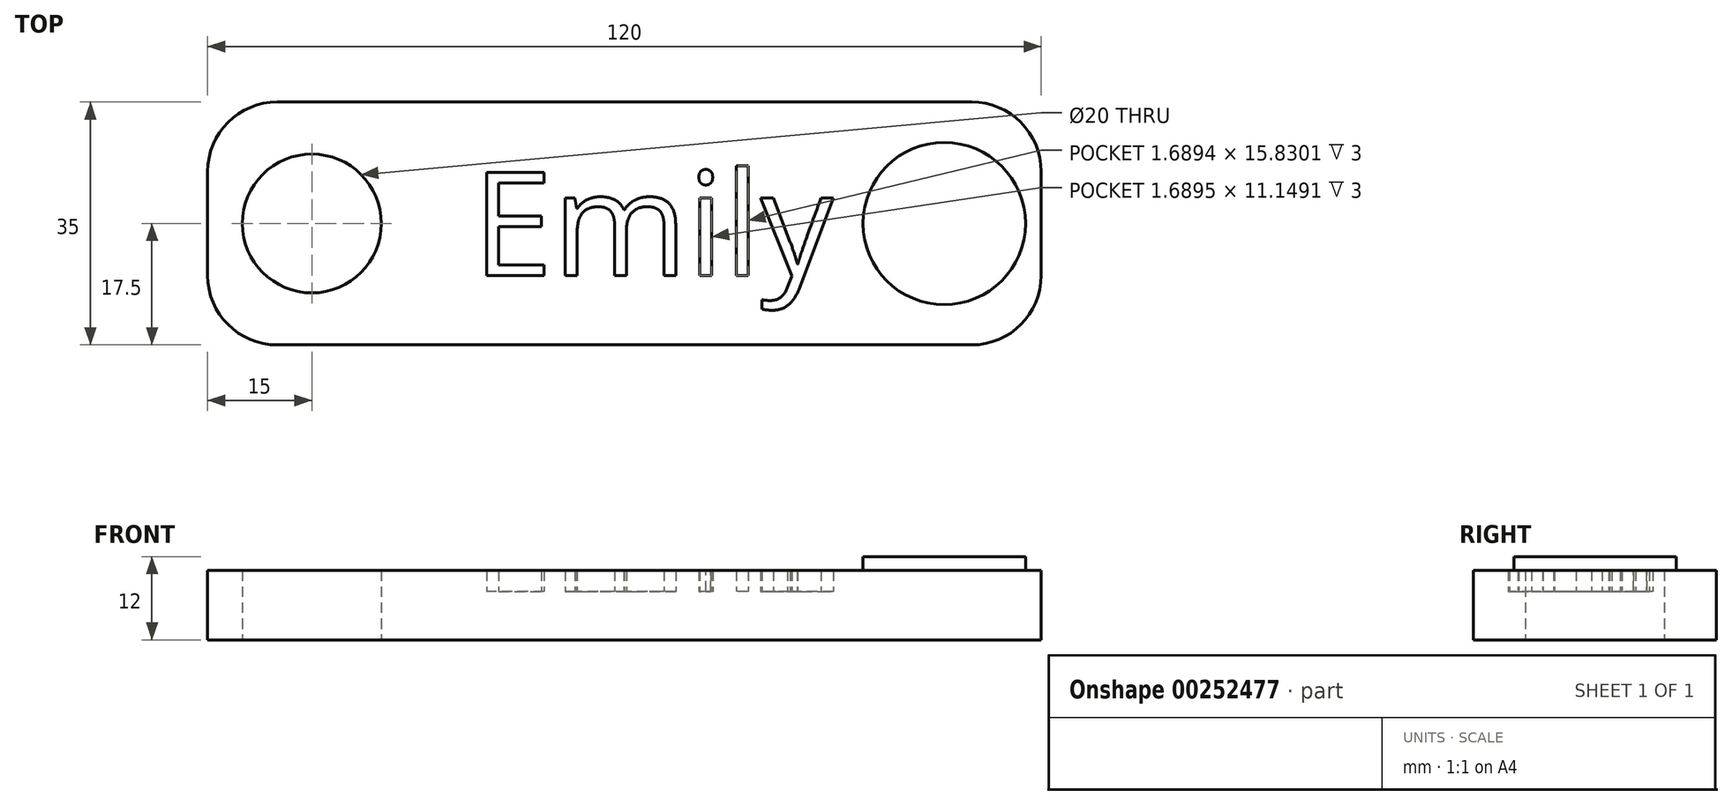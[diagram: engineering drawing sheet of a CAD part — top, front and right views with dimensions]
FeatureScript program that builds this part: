
annotation { "Feature Type Name" : "Feature", "Feature Type Description" : "" }
export const myFeature = defineFeature(function(context is Context, id is Id, definition is map)
    precondition{}
    {
        {
            var Q0;
            Q0=qCreatedBy(makeId("Top.planeOp"),FACE);
            var sketch = newSketch(context, id + "F0", { "sketchPlane" : qUnion([Q0])});
            skLineSegment(sketch, "E0.bottom", {"start": v(60, -17.5) * mm, "end": v(-60, -17.5) * mm});
            skLineSegment(sketch, "E0.top", {"start": v(60, 17.5) * mm, "end": v(-60, 17.5) * mm});
            skLineSegment(sketch, "E0.left", {"start": v(60, -17.5) * mm, "end": v(60, 17.5) * mm});
            skLineSegment(sketch, "E0.right", {"start": v(-60, -17.5) * mm, "end": v(-60, 17.5) * mm});
            skPoint(sketch, "E0.middle", {"position": v(0, 0) * mm});
            skCircle(sketch, "E1", {"center": v(-45, 0) * mm, "radius": 10 * mm});
            skPoint(sketch, "E1.centerSnap0", {"position": v(-60, 0) * mm});
            skSolve(sketch);
        }
        {
            var Q0;
            Q0=makeQuery(id+"F0.imprint","IMPRINT",FACE,{"disambiguationData":[TD([[makeQuery(id+"F0.imprint","IMPRINT",EDGE,{"derivedFrom":sQuery(id+"F0.wireOp",EDGE,"E0.bottom")}),-1.0]])]});
            extrude(context, id + "F1", {"entities" : qUnion([Q0]), "depth" : 5 * mm});
        }
        {
            var Q0;
            Q0=makeQuery(id+"F1.opExtrude","SWEPT_EDGE",EDGE,{"disambiguationData":[OSD([sQuery(id+"F0.wireOp",EDGE,"E0.bottom"),sQuery(id+"F0.wireOp",EDGE,"E0.right")])]});
            var Q1;
            Q1=makeQuery(id+"F1.opExtrude","SWEPT_EDGE",EDGE,{"disambiguationData":[OSD([sQuery(id+"F0.wireOp",EDGE,"E0.bottom"),sQuery(id+"F0.wireOp",EDGE,"E0.left")])]});
            var Q2;
            Q2=makeQuery(id+"F1.opExtrude","SWEPT_EDGE",EDGE,{"disambiguationData":[OSD([sQuery(id+"F0.wireOp",EDGE,"E0.top"),sQuery(id+"F0.wireOp",EDGE,"E0.right")])]});
            var Q3;
            Q3=makeQuery(id+"F1.opExtrude","SWEPT_EDGE",EDGE,{"disambiguationData":[OSD([sQuery(id+"F0.wireOp",EDGE,"E0.top"),sQuery(id+"F0.wireOp",EDGE,"E0.left")])]});
            fillet(context, id + "F2", {"entities" : qUnion([Q0, Q1, Q2, Q3]), "radius" : 10 * mm, "tangentPropagation" : true, "allowEdgeOverflow" : false});
        }
        {
            var Q0;
            Q0=makeQuery(id+"F1.opExtrude","CAP_FACE",FACE,{"disambiguationData":[OSD([sQuery(id+"F0.wireOp",EDGE,"E0.bottom"),sQuery(id+"F0.wireOp",EDGE,"E0.top"),sQuery(id+"F0.wireOp",EDGE,"E0.left"),sQuery(id+"F0.wireOp",EDGE,"E0.right"),sQuery(id+"F0.wireOp",EDGE,"E1")])],"isStart":false});
            var sketch = newSketch(context, id + "F3", { "sketchPlane" : qUnion([Q0])});
            skText(sketch, "E2", { "text": "Emily", "fontName": "OpenSans-Regular.ttf"});
            const initialGuessF3  = {"E2": [-0.02189, -0.0075, 1, 0, 0.015]};
            skSetInitialGuess(sketch, initialGuessF3);
            skSolve(sketch);
        }
        {
            var Q0;
            Q0 = qSketchRegion(id + "F3", true);
            extrude(context, id + "F4", {"entities" : qUnion([Q0]), "operationType" : NewBodyOperationType.ADD, "depth" : 2 * mm});
        }
        {
            var Q0;
            Q0=makeQuery(id+"F1.opExtrude","CAP_FACE",FACE,{"disambiguationData":[OSD([sQuery(id+"F0.wireOp",EDGE,"E0.bottom"),sQuery(id+"F0.wireOp",EDGE,"E0.top"),sQuery(id+"F0.wireOp",EDGE,"E0.left"),sQuery(id+"F0.wireOp",EDGE,"E0.right"),sQuery(id+"F0.wireOp",EDGE,"E1")])],"isStart":false});
            var sketch = newSketch(context, id + "F5", { "sketchPlane" : qUnion([Q0])});
            skSolve(sketch);
        }
        {
            var Q0;
            Q0 = qSketchRegion(id + "F5", true);
            var Q1;
            {var subQ2=sQuery(id+"F0.wireOp",EDGE,"E1");Q1=makeQuery(id+"F5.imprint","IMPRINT",FACE,{"disambiguationData":[TD([[makeQuery(id+"F5.imprint","IMPRINT",EDGE,{"derivedFrom":makeQuery(id+"F1.opExtrude","CAP_EDGE",EDGE,{"disambiguationData":[OSD([subQ2])],"isStart":false})}),-1.0]])]});}
            extrude(context, id + "F6", {"entities" : qUnion([Q0, Q1]), "operationType" : NewBodyOperationType.ADD, "depth" : 5 * mm});
        }
        {
            var Q0;
            Q0=makeQuery(id+"F6.opExtrude","CAP_FACE",FACE,{"disambiguationData":[OSD([sQuery(id+"F0.wireOp",EDGE,"E0.bottom"),sQuery(id+"F0.wireOp",EDGE,"E0.top"),sQuery(id+"F0.wireOp",EDGE,"E0.left"),sQuery(id+"F0.wireOp",EDGE,"E0.right"),sQuery(id+"F0.wireOp",EDGE,"E1"),sQuery(id+"F3.wireOp",EDGE,"E2.sketch_text.stroke-0"),sQuery(id+"F3.wireOp",EDGE,"E2.sketch_text.stroke-1"),sQuery(id+"F3.wireOp",EDGE,"E2.sketch_text.stroke-2"),sQuery(id+"F3.wireOp",EDGE,"E2.sketch_text.stroke-3"),sQuery(id+"F3.wireOp",EDGE,"E2.sketch_text.stroke-4"),sQuery(id+"F3.wireOp",EDGE,"E2.sketch_text.stroke-5"),sQuery(id+"F3.wireOp",EDGE,"E2.sketch_text.stroke-6"),sQuery(id+"F3.wireOp",EDGE,"E2.sketch_text.stroke-7"),sQuery(id+"F3.wireOp",EDGE,"E2.sketch_text.stroke-8"),sQuery(id+"F3.wireOp",EDGE,"E2.sketch_text.stroke-9"),sQuery(id+"F3.wireOp",EDGE,"E2.sketch_text.stroke-10"),sQuery(id+"F3.wireOp",EDGE,"E2.sketch_text.stroke-11"),sQuery(id+"F3.wireOp",EDGE,"E2.sketch_text.stroke-12"),sQuery(id+"F3.wireOp",EDGE,"E2.sketch_text.stroke-13"),sQuery(id+"F3.wireOp",EDGE,"E2.sketch_text.stroke-14"),sQuery(id+"F3.wireOp",EDGE,"E2.sketch_text.stroke-15"),sQuery(id+"F3.wireOp",EDGE,"E2.sketch_text.stroke-16"),sQuery(id+"F3.wireOp",EDGE,"E2.sketch_text.stroke-17"),sQuery(id+"F3.wireOp",EDGE,"E2.sketch_text.stroke-18"),sQuery(id+"F3.wireOp",EDGE,"E2.sketch_text.stroke-19"),sQuery(id+"F3.wireOp",EDGE,"E2.sketch_text.stroke-20"),sQuery(id+"F3.wireOp",EDGE,"E2.sketch_text.stroke-21"),sQuery(id+"F3.wireOp",EDGE,"E2.sketch_text.stroke-22"),sQuery(id+"F3.wireOp",EDGE,"E2.sketch_text.stroke-23"),sQuery(id+"F3.wireOp",EDGE,"E2.sketch_text.stroke-24"),sQuery(id+"F3.wireOp",EDGE,"E2.sketch_text.stroke-25"),sQuery(id+"F3.wireOp",EDGE,"E2.sketch_text.stroke-26"),sQuery(id+"F3.wireOp",EDGE,"E2.sketch_text.stroke-27"),sQuery(id+"F3.wireOp",EDGE,"E2.sketch_text.stroke-28"),sQuery(id+"F3.wireOp",EDGE,"E2.sketch_text.stroke-29"),sQuery(id+"F3.wireOp",EDGE,"E2.sketch_text.stroke-30"),sQuery(id+"F3.wireOp",EDGE,"E2.sketch_text.stroke-31"),sQuery(id+"F3.wireOp",EDGE,"E2.sketch_text.stroke-32"),sQuery(id+"F3.wireOp",EDGE,"E2.sketch_text.stroke-33"),sQuery(id+"F3.wireOp",EDGE,"E2.sketch_text.stroke-34"),sQuery(id+"F3.wireOp",EDGE,"E2.sketch_text.stroke-35"),sQuery(id+"F3.wireOp",EDGE,"E2.sketch_text.stroke-36"),sQuery(id+"F3.wireOp",EDGE,"E2.sketch_text.stroke-37"),sQuery(id+"F3.wireOp",EDGE,"E2.sketch_text.stroke-38"),sQuery(id+"F3.wireOp",EDGE,"E2.sketch_text.stroke-39"),sQuery(id+"F3.wireOp",EDGE,"E2.sketch_text.stroke-40"),sQuery(id+"F3.wireOp",EDGE,"E2.sketch_text.stroke-41"),sQuery(id+"F3.wireOp",EDGE,"E2.sketch_text.stroke-42"),sQuery(id+"F3.wireOp",EDGE,"E2.sketch_text.stroke-43"),sQuery(id+"F3.wireOp",EDGE,"E2.sketch_text.stroke-44"),sQuery(id+"F3.wireOp",EDGE,"E2.sketch_text.stroke-45"),sQuery(id+"F3.wireOp",EDGE,"E2.sketch_text.stroke-46"),sQuery(id+"F3.wireOp",EDGE,"E2.sketch_text.stroke-47"),sQuery(id+"F3.wireOp",EDGE,"E2.sketch_text.stroke-48"),sQuery(id+"F3.wireOp",EDGE,"E2.sketch_text.stroke-49"),sQuery(id+"F3.wireOp",EDGE,"E2.sketch_text.stroke-50"),sQuery(id+"F3.wireOp",EDGE,"E2.sketch_text.stroke-51"),sQuery(id+"F3.wireOp",EDGE,"E2.sketch_text.stroke-52"),sQuery(id+"F3.wireOp",EDGE,"E2.sketch_text.stroke-53"),sQuery(id+"F3.wireOp",EDGE,"E2.sketch_text.stroke-54"),sQuery(id+"F3.wireOp",EDGE,"E2.sketch_text.stroke-55"),sQuery(id+"F3.wireOp",EDGE,"E2.sketch_text.stroke-56"),sQuery(id+"F3.wireOp",EDGE,"E2.sketch_text.stroke-57"),sQuery(id+"F3.wireOp",EDGE,"E2.sketch_text.stroke-58"),sQuery(id+"F3.wireOp",EDGE,"E2.sketch_text.stroke-59"),sQuery(id+"F3.wireOp",EDGE,"E2.sketch_text.stroke-60"),sQuery(id+"F3.wireOp",EDGE,"E2.sketch_text.stroke-61"),sQuery(id+"F3.wireOp",EDGE,"E2.sketch_text.stroke-62"),sQuery(id+"F3.wireOp",EDGE,"E2.sketch_text.stroke-63"),sQuery(id+"F3.wireOp",EDGE,"E2.sketch_text.stroke-64"),sQuery(id+"F3.wireOp",EDGE,"E2.sketch_text.stroke-65"),sQuery(id+"F3.wireOp",EDGE,"E2.sketch_text.stroke-66"),sQuery(id+"F3.wireOp",EDGE,"E2.sketch_text.stroke-67"),sQuery(id+"F3.wireOp",EDGE,"E2.sketch_text.stroke-68"),sQuery(id+"F3.wireOp",EDGE,"E2.sketch_text.stroke-69"),sQuery(id+"F3.wireOp",EDGE,"E2.sketch_text.stroke-70"),sQuery(id+"F3.wireOp",EDGE,"E2.sketch_text.stroke-71")])],"isStart":false});
            var sketch = newSketch(context, id + "F7", { "sketchPlane" : qUnion([Q0])});
            skCircle(sketch, "E3", {"center": v(46.05, 0) * mm, "radius": 11.69 * mm});
            skSolve(sketch);
        }
        {
            var Q0;
            Q0=makeQuery(id+"F7.imprint","IMPRINT",FACE,{"disambiguationData":[TD([[makeQuery(id+"F7.imprint","IMPRINT",EDGE,{"derivedFrom":sQuery(id+"F7.wireOp",EDGE,"E3")}),1.0]])]});
            extrude(context, id + "F8", {"entities" : qUnion([Q0]), "operationType" : NewBodyOperationType.ADD, "depth" : 2 * mm});
        }
    });
